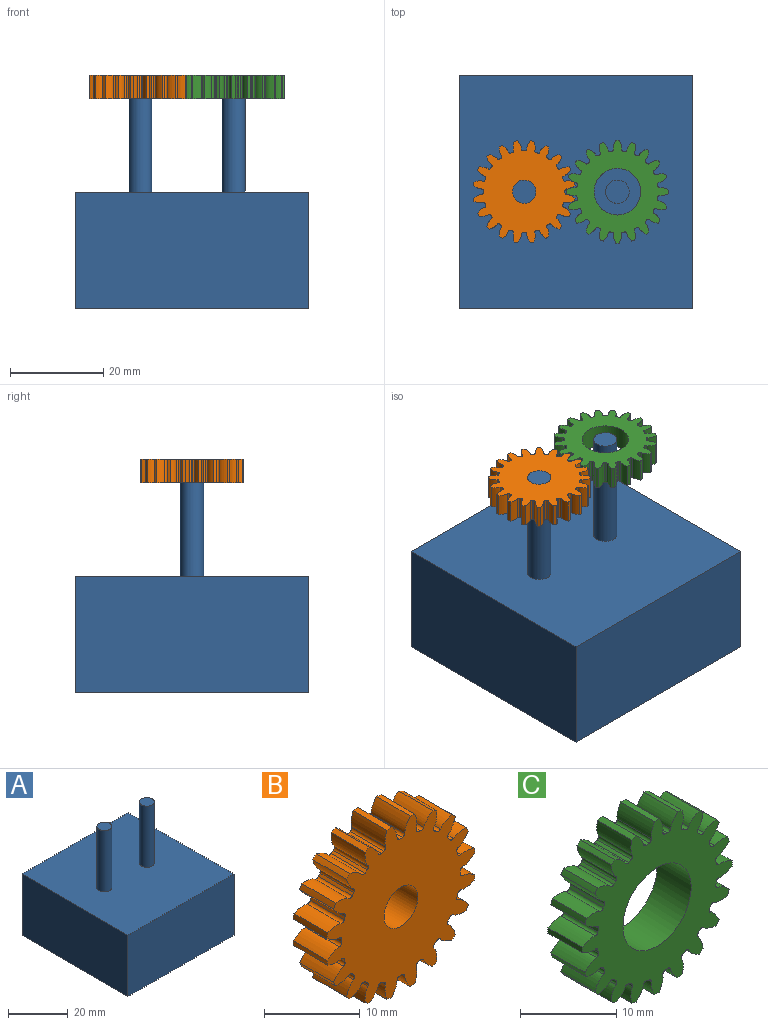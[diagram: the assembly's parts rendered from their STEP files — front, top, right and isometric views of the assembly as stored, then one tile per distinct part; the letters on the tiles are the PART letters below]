
ASSEMBLY  parts=3 mates=2
PART A: 10 faces, bbox 50x50x50 mm
  f0: plane 50x25mm, normal (-1,0,0), area 1250mm2, adj f1,f3,f4,f5
  f1: plane 50x25mm, normal (0,-1,0), area 1250mm2, adj f0,f2,f4,f5
  f2: plane 50x25mm, normal (1,0,0), area 1250mm2, adj f1,f3,f4,f5
  f3: plane 50x25mm, normal (0,1,0), area 1250mm2, adj f0,f2,f4,f5
  f4: plane 50x50mm, normal (0,0,1), area 2460.7mm2, adj f0,f1,f2,f3,f6,f8
  f5: plane 50x50mm, normal (0,0,-1), area 2500mm2, adj f0,f1,f2,f3
  f6: cylinder r=2.5mm len=25mm, axis (0,0,-1), area 392.7mm2, adj f4,f7
  f7: plane 5x5mm, normal (0,0,1), area 19.6mm2, adj f6
  f8: cylinder r=2.5mm len=25mm, axis (0,0,-1), area 392.7mm2, adj f4,f9
  f9: plane 5x5mm, normal (0,0,1), area 19.6mm2, adj f8
PART B: 123 faces, bbox 21.8x5x21.8 mm
  f0: extruded ~5x1.82mm, area 10.1mm2, adj f80,f81,f82,f83
  f1: cylinder r=8.75mm len=5mm, axis (0,1,0), area 2mm2, adj f81,f82,f83,f84
  f2: extruded ~5x1.82mm, area 10.1mm2, adj f3,f81,f82,f84
  f3: cylinder r=11mm len=5mm, axis (0,1,0), area 3.5mm2, adj f2,f4,f81,f82
  f4: extruded ~5x1.98mm, area 10.1mm2, adj f3,f81,f82,f85
  f5: cylinder r=8.75mm len=5mm, axis (0,1,0), area 2mm2, adj f81,f82,f85,f86
  f6: extruded ~5x1.48mm, area 10.1mm2, adj f7,f81,f82,f86
  f7: cylinder r=11mm len=5mm, axis (0,1,0), area 3.5mm2, adj f6,f8,f81,f82
  f8: extruded ~5x1.94mm, area 10.1mm2, adj f7,f81,f82,f87
  f9: cylinder r=8.75mm len=5mm, axis (0,1,0), area 2mm2, adj f81,f82,f87,f88
  f10: extruded ~5x1.71mm, area 10.1mm2, adj f11,f81,f82,f88
  f11: cylinder r=11mm len=5mm, axis (0,1,0), area 3.5mm2, adj f10,f12,f81,f82
  f12: extruded ~5x1.71mm, area 10.1mm2, adj f11,f81,f82,f89
  f13: cylinder r=8.75mm len=5mm, axis (0,1,0), area 2mm2, adj f81,f82,f89,f90
  f14: extruded ~5x1.94mm, area 10.1mm2, adj f15,f81,f82,f90
  f15: cylinder r=11mm len=5mm, axis (0,1,0), area 3.5mm2, adj f14,f16,f81,f82
  f16: extruded ~5x1.48mm, area 10.1mm2, adj f15,f81,f82,f91
  f17: cylinder r=8.75mm len=5mm, axis (0,1,0), area 2mm2, adj f81,f82,f91,f92
  f18: extruded ~5x1.98mm, area 10.1mm2, adj f19,f81,f82,f92
  f19: cylinder r=11mm len=5mm, axis (0,1,0), area 3.5mm2, adj f18,f20,f81,f82
  f20: extruded ~5x1.82mm, area 10.1mm2, adj f19,f81,f82,f93
  f21: cylinder r=8.75mm len=5mm, axis (0,1,0), area 2mm2, adj f81,f82,f93,f94
  f22: extruded ~5x1.82mm, area 10.1mm2, adj f23,f81,f82,f94
  f23: cylinder r=11mm len=5mm, axis (0,1,0), area 3.5mm2, adj f22,f24,f81,f82
  f24: extruded ~5x1.98mm, area 10.1mm2, adj f23,f81,f82,f95
  f25: cylinder r=8.75mm len=5mm, axis (0,1,0), area 2mm2, adj f81,f82,f95,f96
  f26: extruded ~5x1.48mm, area 10.1mm2, adj f27,f81,f82,f96
  f27: cylinder r=11mm len=5mm, axis (0,1,0), area 3.5mm2, adj f26,f28,f81,f82
  f28: extruded ~5x1.94mm, area 10.1mm2, adj f27,f81,f82,f97
  f29: cylinder r=8.75mm len=5mm, axis (0,1,0), area 2mm2, adj f81,f82,f97,f98
  f30: extruded ~5x1.71mm, area 10.1mm2, adj f31,f81,f82,f98
  f31: cylinder r=11mm len=5mm, axis (0,1,0), area 3.5mm2, adj f30,f32,f81,f82
  f32: extruded ~5x1.71mm, area 10.1mm2, adj f31,f81,f82,f99
  f33: cylinder r=8.75mm len=5mm, axis (0,1,0), area 2mm2, adj f81,f82,f99,f100
  f34: extruded ~5x1.94mm, area 10.1mm2, adj f35,f81,f82,f100
  f35: cylinder r=11mm len=5mm, axis (0,1,0), area 3.5mm2, adj f34,f36,f81,f82
  f36: extruded ~5x1.48mm, area 10.1mm2, adj f35,f81,f82,f101
  f37: cylinder r=8.75mm len=5mm, axis (0,1,0), area 2mm2, adj f81,f82,f101,f102
  f38: extruded ~5x1.98mm, area 10.1mm2, adj f39,f81,f82,f102
  f39: cylinder r=11mm len=5mm, axis (0,1,0), area 3.5mm2, adj f38,f40,f81,f82
  f40: extruded ~5x1.82mm, area 10.1mm2, adj f39,f81,f82,f103
  f41: cylinder r=8.75mm len=5mm, axis (0,1,0), area 2mm2, adj f81,f82,f103,f104
  f42: extruded ~5x1.82mm, area 10.1mm2, adj f43,f81,f82,f104
  f43: cylinder r=11mm len=5mm, axis (0,1,0), area 3.5mm2, adj f42,f44,f81,f82
  f44: extruded ~5x1.98mm, area 10.1mm2, adj f43,f81,f82,f105
  f45: cylinder r=8.75mm len=5mm, axis (0,1,0), area 2mm2, adj f81,f82,f105,f106
  f46: extruded ~5x1.48mm, area 10.1mm2, adj f47,f81,f82,f106
  f47: cylinder r=11mm len=5mm, axis (0,1,0), area 3.5mm2, adj f46,f48,f81,f82
  f48: extruded ~5x1.94mm, area 10.1mm2, adj f47,f81,f82,f107
  f49: cylinder r=8.75mm len=5mm, axis (0,1,0), area 2mm2, adj f81,f82,f107,f108
  f50: extruded ~5x1.71mm, area 10.1mm2, adj f51,f81,f82,f108
  f51: cylinder r=11mm len=5mm, axis (0,1,0), area 3.5mm2, adj f50,f52,f81,f82
  f52: extruded ~5x1.71mm, area 10.1mm2, adj f51,f81,f82,f109
  f53: cylinder r=8.75mm len=5mm, axis (0,1,0), area 2mm2, adj f81,f82,f109,f110
  f54: extruded ~5x1.94mm, area 10.1mm2, adj f55,f81,f82,f110
  f55: cylinder r=11mm len=5mm, axis (0,1,0), area 3.5mm2, adj f54,f56,f81,f82
  f56: extruded ~5x1.48mm, area 10.1mm2, adj f55,f81,f82,f111
  f57: cylinder r=8.75mm len=5mm, axis (0,1,0), area 2mm2, adj f81,f82,f111,f112
  f58: extruded ~5x1.98mm, area 10.1mm2, adj f59,f81,f82,f112
  f59: cylinder r=11mm len=5mm, axis (0,1,0), area 3.5mm2, adj f58,f60,f81,f82
  f60: extruded ~5x1.82mm, area 10.1mm2, adj f59,f81,f82,f113
  f61: cylinder r=8.75mm len=5mm, axis (0,1,0), area 2mm2, adj f81,f82,f113,f114
  f62: extruded ~5x1.82mm, area 10.1mm2, adj f63,f81,f82,f114
  f63: cylinder r=11mm len=5mm, axis (0,1,0), area 3.5mm2, adj f62,f64,f81,f82
  f64: extruded ~5x1.98mm, area 10.1mm2, adj f63,f81,f82,f115
  f65: cylinder r=8.75mm len=5mm, axis (0,1,0), area 2mm2, adj f81,f82,f115,f116
  f66: extruded ~5x1.48mm, area 10.1mm2, adj f67,f81,f82,f116
  f67: cylinder r=11mm len=5mm, axis (0,1,0), area 3.5mm2, adj f66,f68,f81,f82
  f68: extruded ~5x1.94mm, area 10.1mm2, adj f67,f81,f82,f117
  f69: cylinder r=8.75mm len=5mm, axis (0,1,0), area 2mm2, adj f81,f82,f117,f118
  f70: extruded ~5x1.71mm, area 10.1mm2, adj f71,f81,f82,f118
  f71: cylinder r=11mm len=5mm, axis (0,1,0), area 3.5mm2, adj f70,f72,f81,f82
  f72: extruded ~5x1.71mm, area 10.1mm2, adj f71,f81,f82,f119
  f73: cylinder r=8.75mm len=5mm, axis (0,1,0), area 2mm2, adj f81,f82,f119,f120
  f74: extruded ~5x1.94mm, area 10.1mm2, adj f75,f81,f82,f120
  f75: cylinder r=11mm len=5mm, axis (0,1,0), area 3.5mm2, adj f74,f76,f81,f82
  f76: extruded ~5x1.48mm, area 10.1mm2, adj f75,f81,f82,f121
  f77: cylinder r=8.75mm len=5mm, axis (0,1,0), area 2mm2, adj f81,f82,f121,f122
  f78: extruded ~5x1.98mm, area 10.1mm2, adj f80,f81,f82,f122
  f79: cylinder r=2.5mm len=5mm, axis (0,1,0), area 78.5mm2, adj f81,f82
  f80: cylinder r=11mm len=5mm, axis (0,1,0), area 3.5mm2, adj f0,f78,f81,f82
  f81: plane 21.84x21.84mm, normal (0,-1,0), area 288mm2, adj f0,f1,f2,f3,f4,f5,f6,f7
  f82: plane 21.84x21.84mm, normal (0,1,0), area 288mm2, adj f0,f1,f2,f3,f4,f5,f6,f7
  f83: cylinder r=0.37mm len=5mm, axis (0,1,0), area 2.8mm2, adj f0,f1,f81,f82
  f84: cylinder r=0.37mm len=5mm, axis (0,1,0), area 2.8mm2, adj f1,f2,f81,f82
  f85: cylinder r=0.37mm len=5mm, axis (0,1,0), area 2.8mm2, adj f4,f5,f81,f82
  f86: cylinder r=0.37mm len=5mm, axis (0,1,0), area 2.8mm2, adj f5,f6,f81,f82
  f87: cylinder r=0.37mm len=5mm, axis (0,1,0), area 2.8mm2, adj f8,f9,f81,f82
  f88: cylinder r=0.37mm len=5mm, axis (0,1,0), area 2.8mm2, adj f9,f10,f81,f82
  f89: cylinder r=0.37mm len=5mm, axis (0,1,0), area 2.8mm2, adj f12,f13,f81,f82
  f90: cylinder r=0.37mm len=5mm, axis (0,1,0), area 2.8mm2, adj f13,f14,f81,f82
  f91: cylinder r=0.37mm len=5mm, axis (0,1,0), area 2.8mm2, adj f16,f17,f81,f82
  f92: cylinder r=0.37mm len=5mm, axis (0,1,0), area 2.8mm2, adj f17,f18,f81,f82
  f93: cylinder r=0.37mm len=5mm, axis (0,1,0), area 2.8mm2, adj f20,f21,f81,f82
  f94: cylinder r=0.37mm len=5mm, axis (0,1,0), area 2.8mm2, adj f21,f22,f81,f82
  f95: cylinder r=0.37mm len=5mm, axis (0,1,0), area 2.8mm2, adj f24,f25,f81,f82
  f96: cylinder r=0.37mm len=5mm, axis (0,1,0), area 2.8mm2, adj f25,f26,f81,f82
  f97: cylinder r=0.37mm len=5mm, axis (0,1,0), area 2.8mm2, adj f28,f29,f81,f82
  f98: cylinder r=0.37mm len=5mm, axis (0,1,0), area 2.8mm2, adj f29,f30,f81,f82
  f99: cylinder r=0.37mm len=5mm, axis (0,1,0), area 2.8mm2, adj f32,f33,f81,f82
  f100: cylinder r=0.37mm len=5mm, axis (0,1,0), area 2.8mm2, adj f33,f34,f81,f82
  f101: cylinder r=0.37mm len=5mm, axis (0,1,0), area 2.8mm2, adj f36,f37,f81,f82
  f102: cylinder r=0.37mm len=5mm, axis (0,1,0), area 2.8mm2, adj f37,f38,f81,f82
  f103: cylinder r=0.37mm len=5mm, axis (0,1,0), area 2.8mm2, adj f40,f41,f81,f82
  f104: cylinder r=0.37mm len=5mm, axis (0,1,0), area 2.8mm2, adj f41,f42,f81,f82
  f105: cylinder r=0.37mm len=5mm, axis (0,1,0), area 2.8mm2, adj f44,f45,f81,f82
  f106: cylinder r=0.37mm len=5mm, axis (0,1,0), area 2.8mm2, adj f45,f46,f81,f82
  f107: cylinder r=0.37mm len=5mm, axis (0,1,0), area 2.8mm2, adj f48,f49,f81,f82
  f108: cylinder r=0.37mm len=5mm, axis (0,1,0), area 2.8mm2, adj f49,f50,f81,f82
  f109: cylinder r=0.37mm len=5mm, axis (0,1,0), area 2.8mm2, adj f52,f53,f81,f82
  f110: cylinder r=0.37mm len=5mm, axis (0,1,0), area 2.8mm2, adj f53,f54,f81,f82
  f111: cylinder r=0.37mm len=5mm, axis (0,1,0), area 2.8mm2, adj f56,f57,f81,f82
  f112: cylinder r=0.37mm len=5mm, axis (0,1,0), area 2.8mm2, adj f57,f58,f81,f82
  f113: cylinder r=0.37mm len=5mm, axis (0,1,0), area 2.8mm2, adj f60,f61,f81,f82
  f114: cylinder r=0.37mm len=5mm, axis (0,1,0), area 2.8mm2, adj f61,f62,f81,f82
  f115: cylinder r=0.37mm len=5mm, axis (0,1,0), area 2.8mm2, adj f64,f65,f81,f82
  f116: cylinder r=0.37mm len=5mm, axis (0,1,0), area 2.8mm2, adj f65,f66,f81,f82
  f117: cylinder r=0.37mm len=5mm, axis (0,1,0), area 2.8mm2, adj f68,f69,f81,f82
  f118: cylinder r=0.37mm len=5mm, axis (0,1,0), area 2.8mm2, adj f69,f70,f81,f82
  f119: cylinder r=0.37mm len=5mm, axis (0,1,0), area 2.8mm2, adj f72,f73,f81,f82
  f120: cylinder r=0.37mm len=5mm, axis (0,1,0), area 2.8mm2, adj f73,f74,f81,f82
  f121: cylinder r=0.37mm len=5mm, axis (0,1,0), area 2.8mm2, adj f76,f77,f81,f82
  f122: cylinder r=0.37mm len=5mm, axis (0,1,0), area 2.8mm2, adj f77,f78,f81,f82
PART C: 123 faces, bbox 22x5x22 mm
  f0: extruded ~5x1.92mm, area 10.1mm2, adj f79,f80,f81,f82
  f1: cylinder r=8.75mm len=5mm, axis (0,1,0), area 2mm2, adj f80,f81,f82,f83
  f2: extruded ~5x1.67mm, area 10.1mm2, adj f3,f80,f81,f83
  f3: cylinder r=11mm len=5mm, axis (0,1,0), area 3.5mm2, adj f2,f4,f80,f81
  f4: extruded ~5x1.98mm, area 10.1mm2, adj f3,f80,f81,f84
  f5: cylinder r=8.75mm len=5mm, axis (0,1,0), area 2mm2, adj f80,f81,f84,f85
  f6: extruded ~5x1.54mm, area 10.1mm2, adj f7,f80,f81,f85
  f7: cylinder r=11mm len=5mm, axis (0,1,0), area 3.5mm2, adj f6,f8,f80,f81
  f8: extruded ~5x1.85mm, area 10.1mm2, adj f7,f80,f81,f86
  f9: cylinder r=8.75mm len=5mm, axis (0,1,0), area 2mm2, adj f80,f81,f86,f87
  f10: extruded ~5x1.85mm, area 10.1mm2, adj f11,f80,f81,f87
  f11: cylinder r=11mm len=5mm, axis (0,1,0), area 3.5mm2, adj f10,f12,f80,f81
  f12: extruded ~5x1.54mm, area 10.1mm2, adj f11,f80,f81,f88
  f13: cylinder r=8.75mm len=5mm, axis (0,1,0), area 2mm2, adj f80,f81,f88,f89
  f14: extruded ~5x1.98mm, area 10.1mm2, adj f15,f80,f81,f89
  f15: cylinder r=11mm len=5mm, axis (0,1,0), area 3.5mm2, adj f14,f16,f80,f81
  f16: extruded ~5x1.67mm, area 10.1mm2, adj f15,f80,f81,f90
  f17: cylinder r=8.75mm len=5mm, axis (0,1,0), area 2mm2, adj f80,f81,f90,f91
  f18: extruded ~5x1.92mm, area 10.1mm2, adj f19,f80,f81,f91
  f19: cylinder r=11mm len=5mm, axis (0,1,0), area 3.5mm2, adj f18,f20,f80,f81
  f20: extruded ~5x1.92mm, area 10.1mm2, adj f19,f80,f81,f92
  f21: cylinder r=8.75mm len=5mm, axis (0,1,0), area 2mm2, adj f80,f81,f92,f93
  f22: extruded ~5x1.67mm, area 10.1mm2, adj f23,f80,f81,f93
  f23: cylinder r=11mm len=5mm, axis (0,1,0), area 3.5mm2, adj f22,f24,f80,f81
  f24: extruded ~5x1.98mm, area 10.1mm2, adj f23,f80,f81,f94
  f25: cylinder r=8.75mm len=5mm, axis (0,1,0), area 2mm2, adj f80,f81,f94,f95
  f26: extruded ~5x1.54mm, area 10.1mm2, adj f27,f80,f81,f95
  f27: cylinder r=11mm len=5mm, axis (0,1,0), area 3.5mm2, adj f26,f28,f80,f81
  f28: extruded ~5x1.85mm, area 10.1mm2, adj f27,f80,f81,f96
  f29: cylinder r=8.75mm len=5mm, axis (0,1,0), area 2mm2, adj f80,f81,f96,f97
  f30: extruded ~5x1.85mm, area 10.1mm2, adj f31,f80,f81,f97
  f31: cylinder r=11mm len=5mm, axis (0,1,0), area 3.5mm2, adj f30,f32,f80,f81
  f32: extruded ~5x1.54mm, area 10.1mm2, adj f31,f80,f81,f98
  f33: cylinder r=8.75mm len=5mm, axis (0,1,0), area 2mm2, adj f80,f81,f98,f99
  f34: extruded ~5x1.98mm, area 10.1mm2, adj f35,f80,f81,f99
  f35: cylinder r=11mm len=5mm, axis (0,1,0), area 3.5mm2, adj f34,f36,f80,f81
  f36: extruded ~5x1.67mm, area 10.1mm2, adj f35,f80,f81,f100
  f37: cylinder r=8.75mm len=5mm, axis (0,1,0), area 2mm2, adj f80,f81,f100,f101
  f38: extruded ~5x1.92mm, area 10.1mm2, adj f39,f80,f81,f101
  f39: cylinder r=11mm len=5mm, axis (0,1,0), area 3.5mm2, adj f38,f40,f80,f81
  f40: extruded ~5x1.92mm, area 10.1mm2, adj f39,f80,f81,f102
  f41: cylinder r=8.75mm len=5mm, axis (0,1,0), area 2mm2, adj f80,f81,f102,f103
  f42: extruded ~5x1.67mm, area 10.1mm2, adj f43,f80,f81,f103
  f43: cylinder r=11mm len=5mm, axis (0,1,0), area 3.5mm2, adj f42,f44,f80,f81
  f44: extruded ~5x1.98mm, area 10.1mm2, adj f43,f80,f81,f104
  f45: cylinder r=8.75mm len=5mm, axis (0,1,0), area 2mm2, adj f80,f81,f104,f105
  f46: extruded ~5x1.54mm, area 10.1mm2, adj f47,f80,f81,f105
  f47: cylinder r=11mm len=5mm, axis (0,1,0), area 3.5mm2, adj f46,f48,f80,f81
  f48: extruded ~5x1.85mm, area 10.1mm2, adj f47,f80,f81,f106
  f49: cylinder r=8.75mm len=5mm, axis (0,1,0), area 2mm2, adj f80,f81,f106,f107
  f50: extruded ~5x1.85mm, area 10.1mm2, adj f51,f80,f81,f107
  f51: cylinder r=11mm len=5mm, axis (0,1,0), area 3.5mm2, adj f50,f52,f80,f81
  f52: extruded ~5x1.54mm, area 10.1mm2, adj f51,f80,f81,f108
  f53: cylinder r=8.75mm len=5mm, axis (0,1,0), area 2mm2, adj f80,f81,f108,f109
  f54: extruded ~5x1.98mm, area 10.1mm2, adj f55,f80,f81,f109
  f55: cylinder r=11mm len=5mm, axis (0,1,0), area 3.5mm2, adj f54,f56,f80,f81
  f56: extruded ~5x1.67mm, area 10.1mm2, adj f55,f80,f81,f110
  f57: cylinder r=8.75mm len=5mm, axis (0,1,0), area 2mm2, adj f80,f81,f110,f111
  f58: extruded ~5x1.92mm, area 10.1mm2, adj f59,f80,f81,f111
  f59: cylinder r=11mm len=5mm, axis (0,1,0), area 3.5mm2, adj f58,f60,f80,f81
  f60: extruded ~5x1.92mm, area 10.1mm2, adj f59,f80,f81,f112
  f61: cylinder r=8.75mm len=5mm, axis (0,1,0), area 2mm2, adj f80,f81,f112,f113
  f62: extruded ~5x1.67mm, area 10.1mm2, adj f63,f80,f81,f113
  f63: cylinder r=11mm len=5mm, axis (0,1,0), area 3.5mm2, adj f62,f64,f80,f81
  f64: extruded ~5x1.98mm, area 10.1mm2, adj f63,f80,f81,f114
  f65: cylinder r=8.75mm len=5mm, axis (0,1,0), area 2mm2, adj f80,f81,f114,f115
  f66: extruded ~5x1.54mm, area 10.1mm2, adj f67,f80,f81,f115
  f67: cylinder r=11mm len=5mm, axis (0,1,0), area 3.5mm2, adj f66,f68,f80,f81
  f68: extruded ~5x1.85mm, area 10.1mm2, adj f67,f80,f81,f116
  f69: cylinder r=8.75mm len=5mm, axis (0,1,0), area 2mm2, adj f80,f81,f116,f117
  f70: extruded ~5x1.85mm, area 10.1mm2, adj f71,f80,f81,f117
  f71: cylinder r=11mm len=5mm, axis (0,1,0), area 3.5mm2, adj f70,f72,f80,f81
  f72: extruded ~5x1.54mm, area 10.1mm2, adj f71,f80,f81,f118
  f73: cylinder r=8.75mm len=5mm, axis (0,1,0), area 2mm2, adj f80,f81,f118,f119
  f74: extruded ~5x1.98mm, area 10.1mm2, adj f75,f80,f81,f119
  f75: cylinder r=11mm len=5mm, axis (0,1,0), area 3.5mm2, adj f74,f76,f80,f81
  f76: extruded ~5x1.67mm, area 10.1mm2, adj f75,f80,f81,f120
  f77: cylinder r=8.75mm len=5mm, axis (0,1,0), area 2mm2, adj f80,f81,f120,f121
  f78: extruded ~5x1.92mm, area 10.1mm2, adj f79,f80,f81,f121
  f79: cylinder r=11mm len=5mm, axis (0,1,0), area 3.5mm2, adj f0,f78,f80,f81
  f80: plane 22x22mm, normal (0,-1,0), area 229.1mm2, adj f0,f1,f2,f3,f4,f5,f6,f7
  f81: plane 22x22mm, normal (0,1,0), area 229.1mm2, adj f0,f1,f2,f3,f4,f5,f6,f7
  f82: cylinder r=0.37mm len=5mm, axis (0,1,0), area 2.8mm2, adj f0,f1,f80,f81
  f83: cylinder r=0.37mm len=5mm, axis (0,1,0), area 2.8mm2, adj f1,f2,f80,f81
  f84: cylinder r=0.37mm len=5mm, axis (0,1,0), area 2.8mm2, adj f4,f5,f80,f81
  f85: cylinder r=0.37mm len=5mm, axis (0,1,0), area 2.8mm2, adj f5,f6,f80,f81
  f86: cylinder r=0.37mm len=5mm, axis (0,1,0), area 2.8mm2, adj f8,f9,f80,f81
  f87: cylinder r=0.37mm len=5mm, axis (0,1,0), area 2.8mm2, adj f9,f10,f80,f81
  f88: cylinder r=0.37mm len=5mm, axis (0,1,0), area 2.8mm2, adj f12,f13,f80,f81
  f89: cylinder r=0.37mm len=5mm, axis (0,1,0), area 2.8mm2, adj f13,f14,f80,f81
  f90: cylinder r=0.37mm len=5mm, axis (0,1,0), area 2.8mm2, adj f16,f17,f80,f81
  f91: cylinder r=0.37mm len=5mm, axis (0,1,0), area 2.8mm2, adj f17,f18,f80,f81
  f92: cylinder r=0.37mm len=5mm, axis (0,1,0), area 2.8mm2, adj f20,f21,f80,f81
  f93: cylinder r=0.37mm len=5mm, axis (0,1,0), area 2.8mm2, adj f21,f22,f80,f81
  f94: cylinder r=0.37mm len=5mm, axis (0,1,0), area 2.8mm2, adj f24,f25,f80,f81
  f95: cylinder r=0.37mm len=5mm, axis (0,1,0), area 2.8mm2, adj f25,f26,f80,f81
  f96: cylinder r=0.37mm len=5mm, axis (0,1,0), area 2.8mm2, adj f28,f29,f80,f81
  f97: cylinder r=0.37mm len=5mm, axis (0,1,0), area 2.8mm2, adj f29,f30,f80,f81
  f98: cylinder r=0.37mm len=5mm, axis (0,1,0), area 2.8mm2, adj f32,f33,f80,f81
  f99: cylinder r=0.37mm len=5mm, axis (0,1,0), area 2.8mm2, adj f33,f34,f80,f81
  f100: cylinder r=0.37mm len=5mm, axis (0,1,0), area 2.8mm2, adj f36,f37,f80,f81
  f101: cylinder r=0.37mm len=5mm, axis (0,1,0), area 2.8mm2, adj f37,f38,f80,f81
  f102: cylinder r=0.37mm len=5mm, axis (0,1,0), area 2.8mm2, adj f40,f41,f80,f81
  f103: cylinder r=0.37mm len=5mm, axis (0,1,0), area 2.8mm2, adj f41,f42,f80,f81
  f104: cylinder r=0.37mm len=5mm, axis (0,1,0), area 2.8mm2, adj f44,f45,f80,f81
  f105: cylinder r=0.37mm len=5mm, axis (0,1,0), area 2.8mm2, adj f45,f46,f80,f81
  f106: cylinder r=0.37mm len=5mm, axis (0,1,0), area 2.8mm2, adj f48,f49,f80,f81
  f107: cylinder r=0.37mm len=5mm, axis (0,1,0), area 2.8mm2, adj f49,f50,f80,f81
  f108: cylinder r=0.37mm len=5mm, axis (0,1,0), area 2.8mm2, adj f52,f53,f80,f81
  f109: cylinder r=0.37mm len=5mm, axis (0,1,0), area 2.8mm2, adj f53,f54,f80,f81
  f110: cylinder r=0.37mm len=5mm, axis (0,1,0), area 2.8mm2, adj f56,f57,f80,f81
  f111: cylinder r=0.37mm len=5mm, axis (0,1,0), area 2.8mm2, adj f57,f58,f80,f81
  f112: cylinder r=0.37mm len=5mm, axis (0,1,0), area 2.8mm2, adj f60,f61,f80,f81
  f113: cylinder r=0.37mm len=5mm, axis (0,1,0), area 2.8mm2, adj f61,f62,f80,f81
  f114: cylinder r=0.37mm len=5mm, axis (0,1,0), area 2.8mm2, adj f64,f65,f80,f81
  f115: cylinder r=0.37mm len=5mm, axis (0,1,0), area 2.8mm2, adj f65,f66,f80,f81
  f116: cylinder r=0.37mm len=5mm, axis (0,1,0), area 2.8mm2, adj f68,f69,f80,f81
  f117: cylinder r=0.37mm len=5mm, axis (0,1,0), area 2.8mm2, adj f69,f70,f80,f81
  f118: cylinder r=0.37mm len=5mm, axis (0,1,0), area 2.8mm2, adj f72,f73,f80,f81
  f119: cylinder r=0.37mm len=5mm, axis (0,1,0), area 2.8mm2, adj f73,f74,f80,f81
  f120: cylinder r=0.37mm len=5mm, axis (0,1,0), area 2.8mm2, adj f76,f77,f80,f81
  f121: cylinder r=0.37mm len=5mm, axis (0,1,0), area 2.8mm2, adj f77,f78,f80,f81
  f122: cylinder r=5mm len=10mm, axis (0,1,0), area 157.1mm2, adj f80,f81
PLACE A t=(-29.76,-14.39,-11.56)mm fixed
PLACE B rot(axis=(-1,0,0),90deg) t=(-38.36,-6.77,33.44)mm
PLACE C rot(axis=(-1,0,0),90deg) t=(-18.36,-6.77,33.44)mm
MATE revolute B.f3 <-> A.f6  axis (0,0,1) through (-38.36,-6.77,38.44)mm
MATE revolute C.f3 <-> A.f8  axis (0,0,1) through (-18.36,-6.77,38.44)mm
